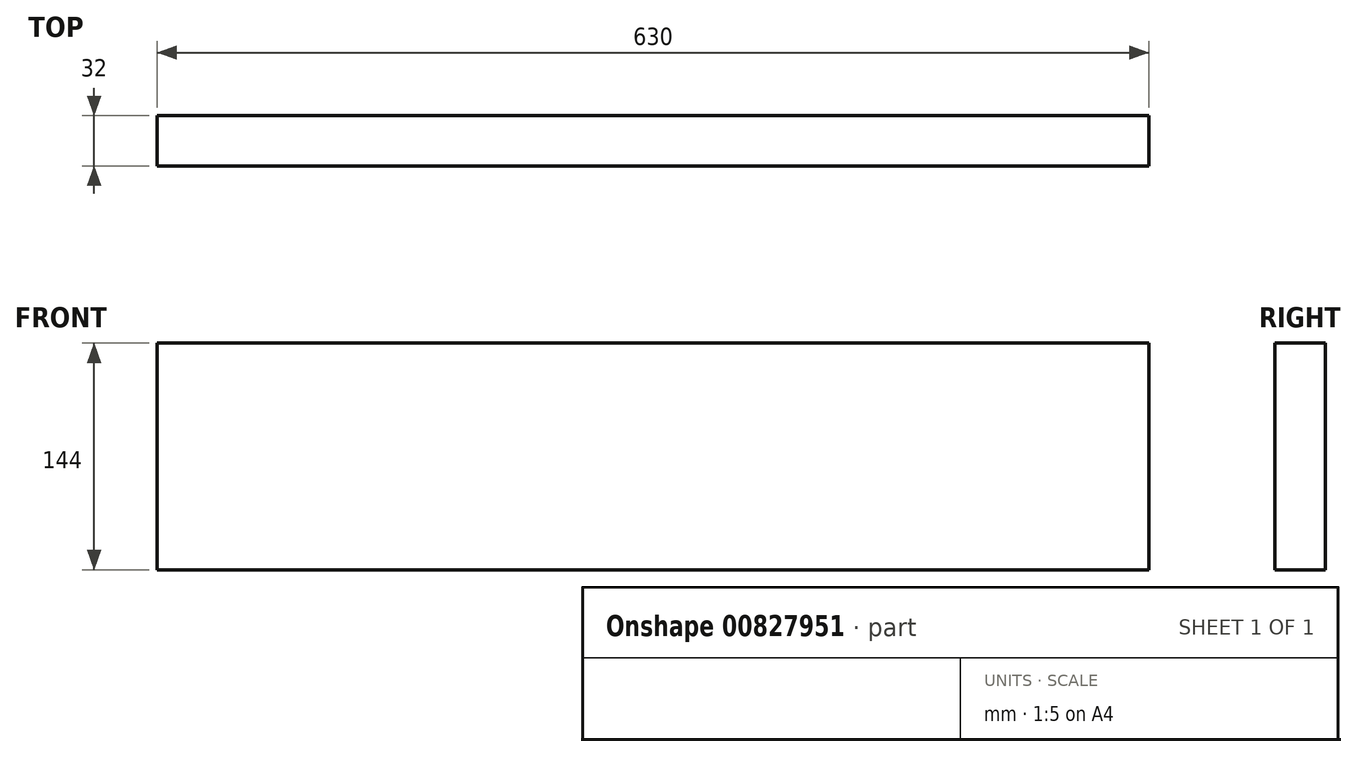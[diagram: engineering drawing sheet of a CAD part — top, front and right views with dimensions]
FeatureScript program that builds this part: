
annotation { "Feature Type Name" : "Feature", "Feature Type Description" : "" }
export const myFeature = defineFeature(function(context is Context, id is Id, definition is map)
    precondition{}
    {
        {
            var Q0;
            Q0=qCreatedBy(makeId("Top.planeOp"),FACE);
            var sketch = newSketch(context, id + "F0", { "sketchPlane" : qUnion([Q0])});
            skLineSegment(sketch, "E0.bottom", {"start": v(-315, 16) * mm, "end": v(315, 16) * mm});
            skLineSegment(sketch, "E0.top", {"start": v(-315, -16) * mm, "end": v(315, -16) * mm});
            skLineSegment(sketch, "E0.left", {"start": v(-315, 16) * mm, "end": v(-315, -16) * mm});
            skLineSegment(sketch, "E0.right", {"start": v(315, 16) * mm, "end": v(315, -16) * mm});
            skPoint(sketch, "E0.middle", {"position": v(0, 0) * mm});
            skSolve(sketch);
        }
        {
            var Q0;
            Q0=makeQuery(id+"F0.imprint","IMPRINT",FACE,{"disambiguationData":[TD([[makeQuery(id+"F0.imprint","IMPRINT",EDGE,{"derivedFrom":sQuery(id+"F0.wireOp",EDGE,"E0.bottom")}),-1.0]])]});
            extrude(context, id + "F1", {"entities" : qUnion([Q0]), "depth" : 144 * mm, "offsetDistance" : 25 * mm});
        }
    });
